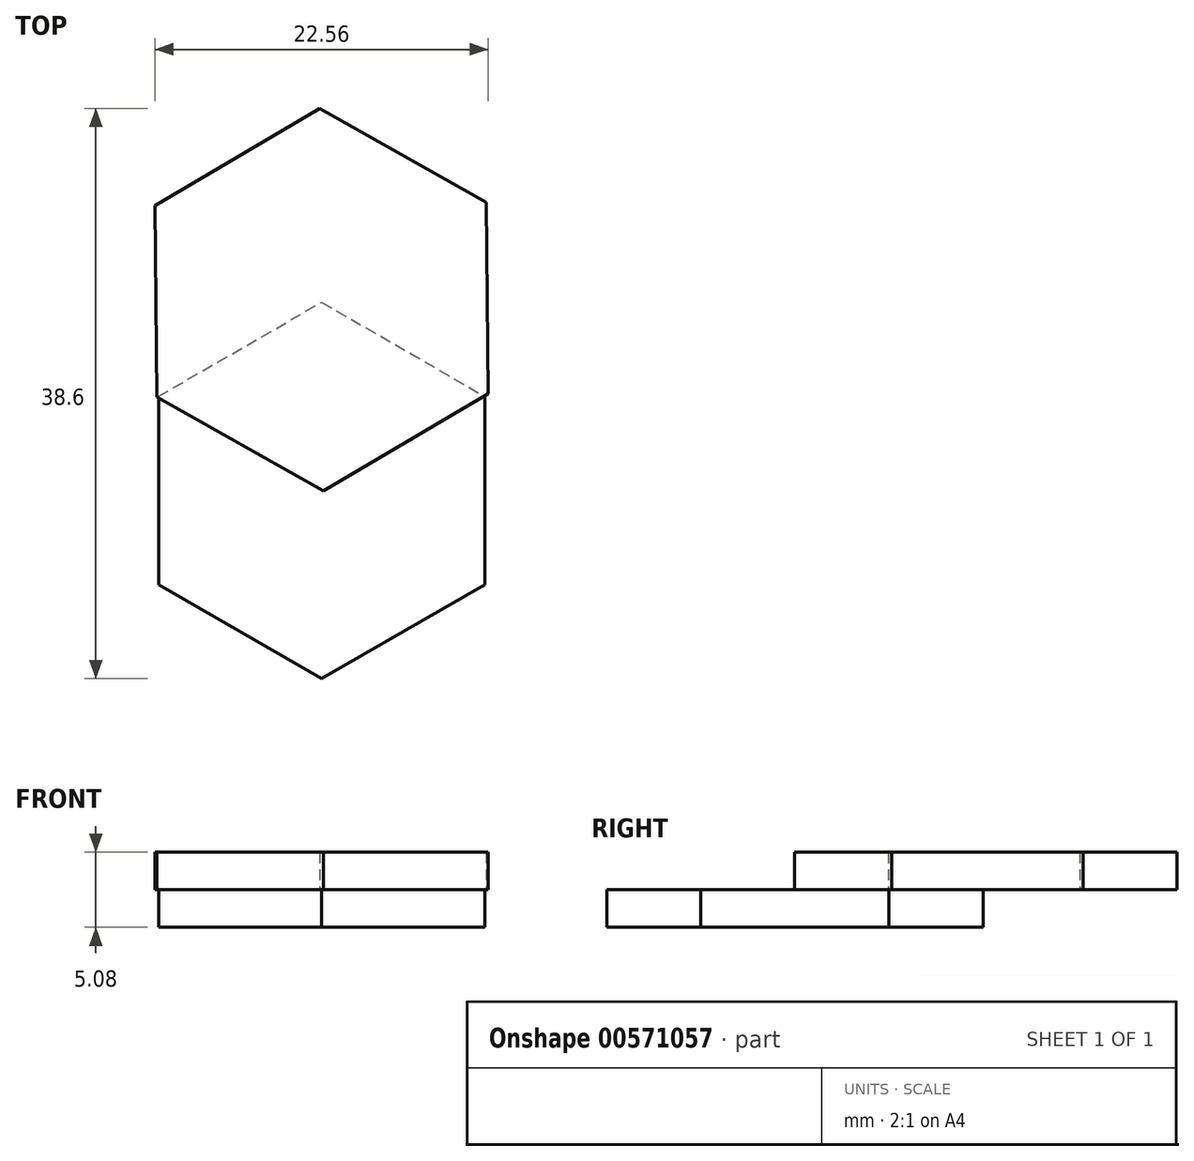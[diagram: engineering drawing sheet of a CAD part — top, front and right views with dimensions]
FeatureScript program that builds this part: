
annotation { "Feature Type Name" : "Feature", "Feature Type Description" : "" }
export const myFeature = defineFeature(function(context is Context, id is Id, definition is map)
    precondition{}
    {
        {
            var Q0;
            Q0=qCreatedBy(makeId("Top.planeOp"),FACE);
            var sketch = newSketch(context, id + "F0", { "sketchPlane" : qUnion([Q0])});
            skCircle(sketch, "E0.cCircle", {"center": v(-23.02, 0) * mm, "radius": 11.03 * mm, "construction": true});
            skLineSegment(sketch, "E0.0", {"start": v(-11.99, 6.37) * mm, "end": v(-11.99, -6.37) * mm});
            skLineSegment(sketch, "E0.1", {"start": v(-11.99, -6.37) * mm, "end": v(-23.02, -12.74) * mm});
            skLineSegment(sketch, "E0.2", {"start": v(-23.02, -12.74) * mm, "end": v(-34.05, -6.37) * mm});
            skLineSegment(sketch, "E0.3", {"start": v(-34.05, -6.37) * mm, "end": v(-34.05, 6.37) * mm});
            skLineSegment(sketch, "E0.4", {"start": v(-34.05, 6.37) * mm, "end": v(-23.02, 12.74) * mm});
            skLineSegment(sketch, "E0.5", {"start": v(-23.02, 12.74) * mm, "end": v(-11.99, 6.37) * mm});
            skPoint(sketch, "E0.0.midPoint", {"position": v(-11.99, 0) * mm});
            skSolve(sketch);
        }
        {
            var Q0;
            Q0=makeQuery(id+"F0.imprint","IMPRINT",FACE,{"disambiguationData":[TD([[makeQuery(id+"F0.imprint","IMPRINT",EDGE,{"derivedFrom":sQuery(id+"F0.wireOp",EDGE,"E0.0")}),-1.0]])]});
            var Q1;
            Q1=sQuery(id+"F0.wireOp",EDGE,"E0.3");
            var Q2;
            Q2=sQuery(id+"F0.wireOp",EDGE,"E0.4");
            var Q3;
            Q3=sQuery(id+"F0.wireOp",EDGE,"E0.5");
            var Q4;
            Q4=sQuery(id+"F0.wireOp",EDGE,"E0.0");
            var Q5;
            Q5=sQuery(id+"F0.wireOp",EDGE,"E0.1");
            var Q6;
            Q6=sQuery(id+"F0.wireOp",EDGE,"E0.2");
            extrude(context, id + "F1", {"entities" : qUnion([Q0]), "surfaceEntities" : qUnion([Q1, Q2, Q3, Q4, Q5, Q6]), "depth" : 2.54 * mm, "offsetDistance" : 25.4 * mm});
        }
        {
            var Q0;
            Q0=makeQuery(id+"F1.opExtrude","CAP_FACE",FACE,{"disambiguationData":[OSD([sQuery(id+"F0.wireOp",EDGE,"E0.0"),sQuery(id+"F0.wireOp",EDGE,"E0.1"),sQuery(id+"F0.wireOp",EDGE,"E0.2"),sQuery(id+"F0.wireOp",EDGE,"E0.3"),sQuery(id+"F0.wireOp",EDGE,"E0.4"),sQuery(id+"F0.wireOp",EDGE,"E0.5")])],"isStart":false});
            var sketch = newSketch(context, id + "F2", { "sketchPlane" : qUnion([Q0])});
            skCircle(sketch, "E1.cCircle", {"center": v(-23.02, 12.91) * mm, "radius": 11.21 * mm, "construction": true});
            skPoint(sketch, "E1.cCircle.perimeterSnap0", {"position": v(-17.5, -9.55) * mm});
            skLineSegment(sketch, "E1.0", {"start": v(-23.14, 25.86) * mm, "end": v(-11.87, 19.5) * mm});
            skLineSegment(sketch, "E1.1", {"start": v(-11.87, 19.5) * mm, "end": v(-11.74, 6.54) * mm});
            skLineSegment(sketch, "E1.2", {"start": v(-11.74, 6.54) * mm, "end": v(-22.9, -0.04) * mm});
            skLineSegment(sketch, "E1.3", {"start": v(-22.9, -0.04) * mm, "end": v(-34.17, 6.33) * mm});
            skLineSegment(sketch, "E1.4", {"start": v(-34.17, 6.33) * mm, "end": v(-34.3, 19.28) * mm});
            skLineSegment(sketch, "E1.5", {"start": v(-34.3, 19.28) * mm, "end": v(-23.14, 25.86) * mm});
            skPoint(sketch, "E1.0.midPoint", {"position": v(-17.5, 22.68) * mm});
            skPoint(sketch, "E1.0.midPoint.positionSnap0", {"position": v(-17.5, -9.55) * mm});
            skSolve(sketch);
        }
        {
            var Q0;
            Q0 = qSketchRegion(id + "F2", true);
            extrude(context, id + "F3", {"entities" : qUnion([Q0]), "operationType" : NewBodyOperationType.ADD, "depth" : 2.54 * mm, "offsetDistance" : 25.4 * mm});
        }
    });
